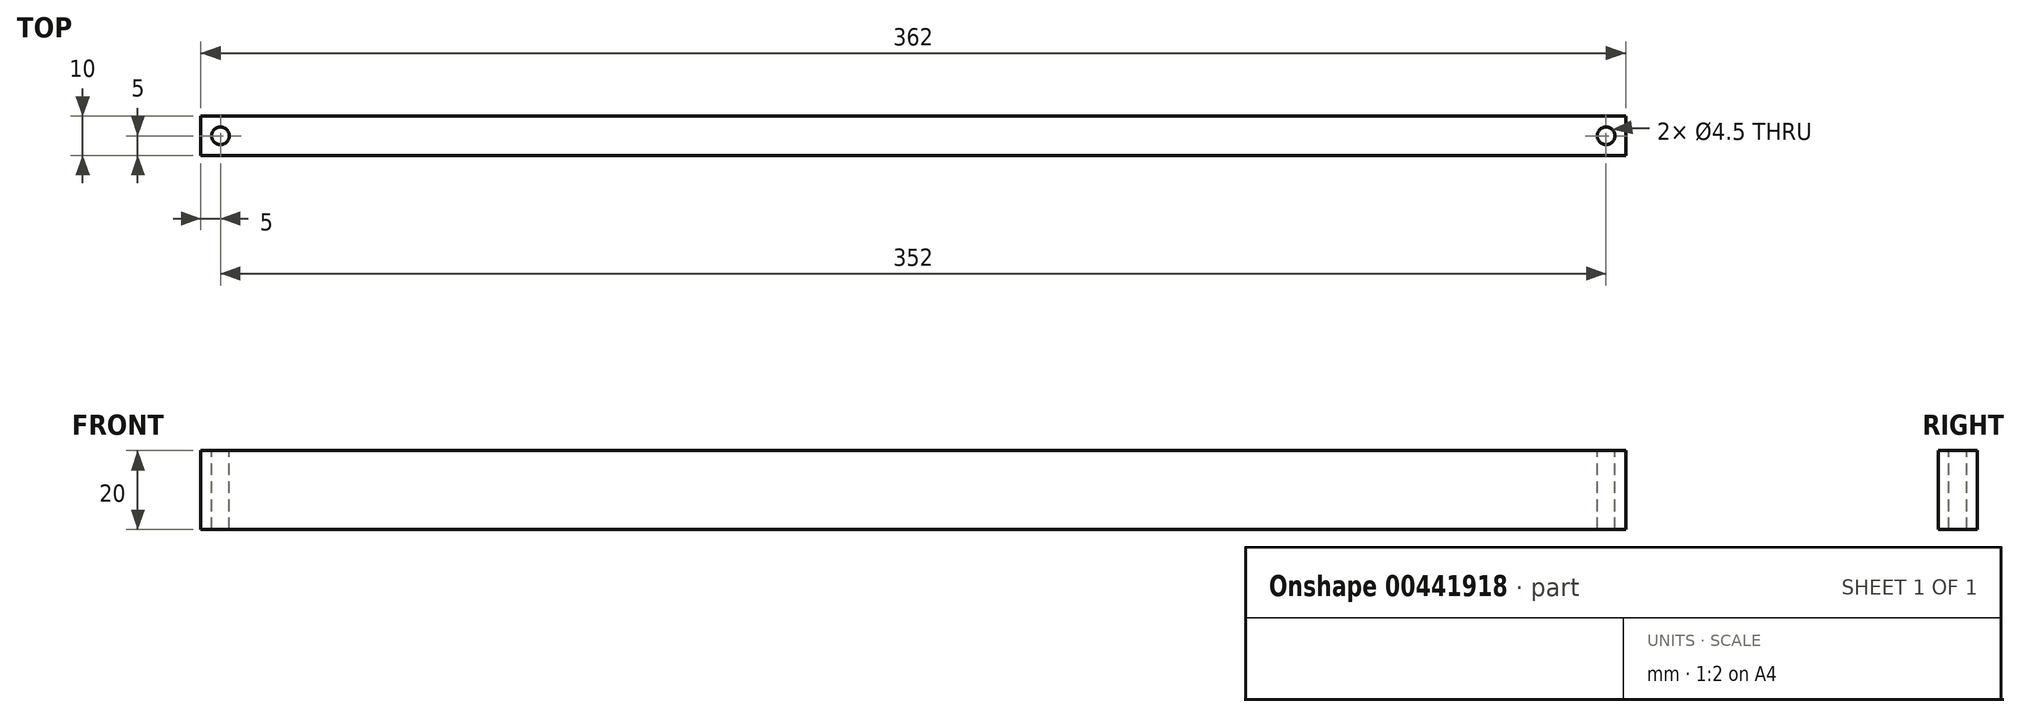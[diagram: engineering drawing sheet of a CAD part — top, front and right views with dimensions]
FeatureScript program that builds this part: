
annotation { "Feature Type Name" : "Feature", "Feature Type Description" : "" }
export const myFeature = defineFeature(function(context is Context, id is Id, definition is map)
    precondition{}
    {
        {
            var Q0;
            Q0=qCreatedBy(makeId("Front.planeOp"),FACE);
            var sketch = newSketch(context, id + "F0", { "sketchPlane" : qUnion([Q0])});
            skLineSegment(sketch, "E0.bottom", {"start": v(-181, -11.36) * mm, "end": v(181, -11.36) * mm});
            skLineSegment(sketch, "E0.top", {"start": v(-181, -31.36) * mm, "end": v(181, -31.36) * mm});
            skLineSegment(sketch, "E0.left", {"start": v(-181, -11.36) * mm, "end": v(-181, -31.36) * mm});
            skLineSegment(sketch, "E0.right", {"start": v(181, -11.36) * mm, "end": v(181, -31.36) * mm});
            skSolve(sketch);
        }
        {
            var Q0;
            Q0=qSketchRegion(id+"F0",true);
            extrude(context, id + "F1", {"entities" : qUnion([Q0]), "depth" : 10 * mm});
        }
        {
            var Q0;
            Q0=makeQuery(id+"F1.opExtrude","SWEPT_FACE",FACE,{"disambiguationData":[OSD([sQuery(id+"F0.wireOp",EDGE,"E0.bottom")])]});
            var sketch = newSketch(context, id + "F2", { "sketchPlane" : qUnion([Q0])});
            skCircle(sketch, "E1", {"center": v(-176, -5) * mm, "radius": 2.25 * mm});
            skCircle(sketch, "E2", {"center": v(176, -5) * mm, "radius": 2.25 * mm});
            skSolve(sketch);
        }
        {
            var Q0;
            Q0=qSketchRegion(id+"F2",true);
            extrude(context, id + "F3", {"entities" : qUnion([Q0]), "operationType" : NewBodyOperationType.REMOVE, "endBound" : BoundingType.THROUGH_ALL, "oppositeDirection" : true, "depth" : 25 * mm});
        }
    });
